# Revit family: Site_Accessories-Bike_Ovella-Systems-Oy_Junior_V-3_N
name_source: partatom
category: Specialty Equipment
units: mm (PartAtom-declared; Revit-internal decimal feet)

## family parameters
Cut with Voids When Loaded = No
Enable Cutting in Views = Yes
Host = Face
Maintain Annotation Orientation = No
OmniClass Number = 23.11.29.11.11
OmniClass Title = Bicycle Racks
Part Type = Normal
Room Calculation Point = No
Round Connector Dimension = Use Diameter
Shared = No

## types (1)
- Junior - V-3
    Default Elevation = 330 mm
    Distance = 500 mm  [stored 1.64042 ft]
    Height = 280 mm
    Length = 150 mm
    Manufacturer = Ovella Systems Oy
    Model = Junior - V-3
    Product Material = Ovella Systems Oy - Metal - Steel - Black
    Product Page URL = https://www.ovella.fi
    URL = https://www.ovella.fi
    Version = 1
    Width = 90 mm

note: [stored X ft] marks values corroborated as IEEE doubles in the binary element streams (Revit-internal decimal feet)

## geometry (parser evidence)
native form markers: Sweep x6
no freeform markers — native parametric forms only
